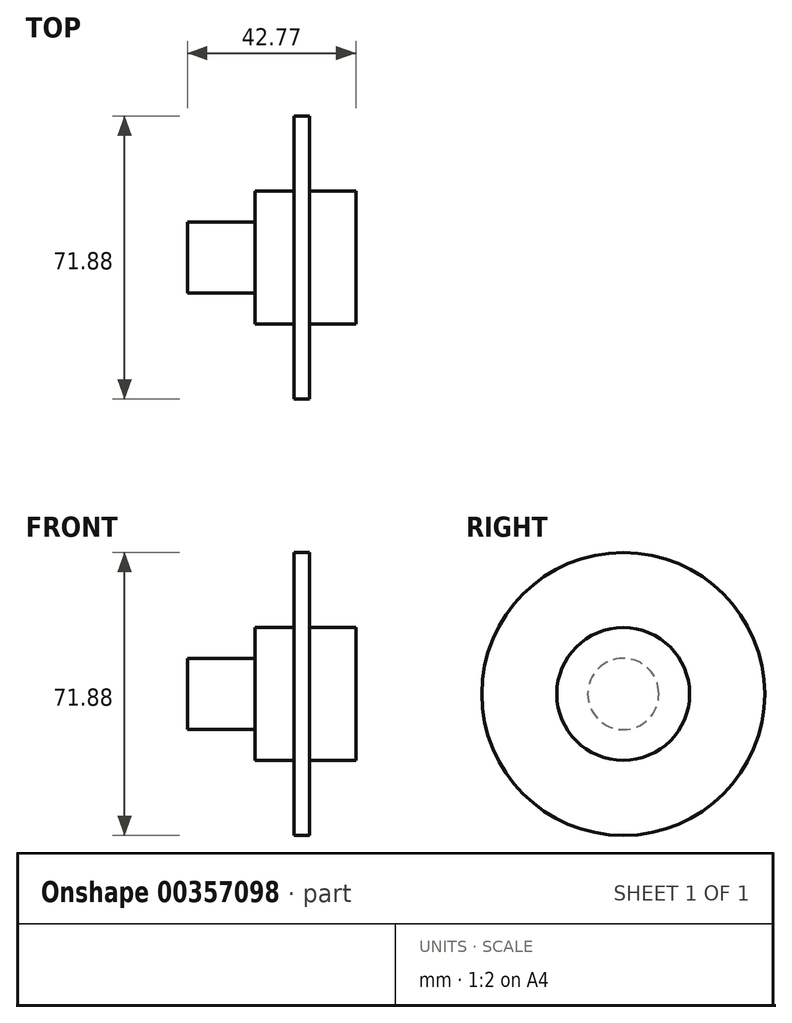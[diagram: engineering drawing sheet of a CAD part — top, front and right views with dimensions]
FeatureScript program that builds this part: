
annotation { "Feature Type Name" : "Feature", "Feature Type Description" : "" }
export const myFeature = defineFeature(function(context is Context, id is Id, definition is map)
    precondition{}
    {
        {
            var Q0;
            Q0=qCreatedBy(makeId("Front.planeOp"),FACE);
            var sketch = newSketch(context, id + "F0", { "sketchPlane" : qUnion([Q0])});
            skLineSegment(sketch, "E0", {"start": v(0, 0) * mm, "end": v(-42.77, 0) * mm});
            skLineSegment(sketch, "E1", {"start": v(-42.77, 0) * mm, "end": v(-42.77, 9.04) * mm});
            skLineSegment(sketch, "E2", {"start": v(0, 0) * mm, "end": v(0, 16.87) * mm});
            skLineSegment(sketch, "E3", {"start": v(0, 16.87) * mm, "end": v(-11.73, 16.87) * mm});
            skLineSegment(sketch, "E4", {"start": v(-11.73, 16.87) * mm, "end": v(-11.73, 35.94) * mm});
            skLineSegment(sketch, "E5", {"start": v(-11.73, 35.94) * mm, "end": v(-15.65, 35.94) * mm});
            skLineSegment(sketch, "E6", {"start": v(-15.65, 35.94) * mm, "end": v(-15.65, 16.87) * mm});
            skLineSegment(sketch, "E7", {"start": v(-15.65, 16.87) * mm, "end": v(-25.63, 16.87) * mm});
            skLineSegment(sketch, "E8", {"start": v(-25.63, 16.87) * mm, "end": v(-25.63, 9.04) * mm});
            skLineSegment(sketch, "E9", {"start": v(-25.63, 9.04) * mm, "end": v(-42.77, 9.04) * mm});
            skSolve(sketch);
        }
        {
            var Q0;
            Q0=makeQuery(id+"F0.imprint","IMPRINT",FACE,{"disambiguationData":[TD([[makeQuery(id+"F0.imprint","IMPRINT",EDGE,{"derivedFrom":sQuery(id+"F0.wireOp",EDGE,"E0")}),-1.0]])]});
            var Q1;
            Q1=sQuery(id+"F0.wireOp",EDGE,"E0");
            revolve(context, id + "F1", {"entities" : qUnion([Q0]), "axis" : qUnion([Q1]), "revolveType" : RevolveType.FULL});
        }
    });
